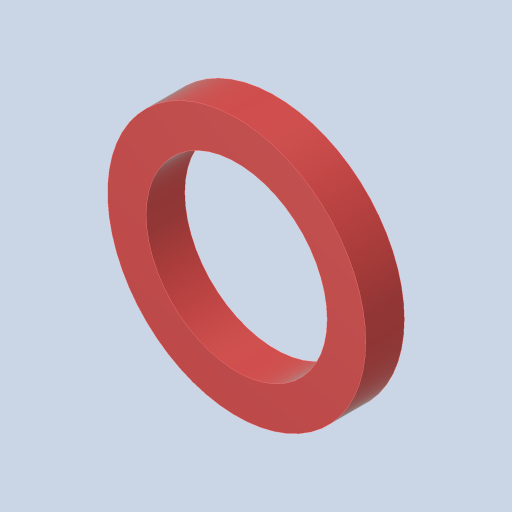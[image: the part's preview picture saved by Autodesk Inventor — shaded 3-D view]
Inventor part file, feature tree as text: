
AUTODESK INVENTOR PART (.ipt)
format: ipt  version: 2023.4 (Build 274418000, 418)  size: 108,544 bytes
history: native  units: in
note: dims shown in document units (in); Inventor stores cm internally (conversion verified against a paired STEP export)
features: extrude x1, sketch x1
ambient origin geometry x8: Origin, YZ Plane, XZ Plane, XY Plane, X Axis, Y Axis, Z Axis, Center Point
bodies: Solid1 (feature_tree)
feature tree (2):
  extrude  "Extrusion1"  Depth=0.125in
  sketch  "Sketch1"  dims[d0=0.585in d1=0.125in d2=0.125in d3=0.0in]
